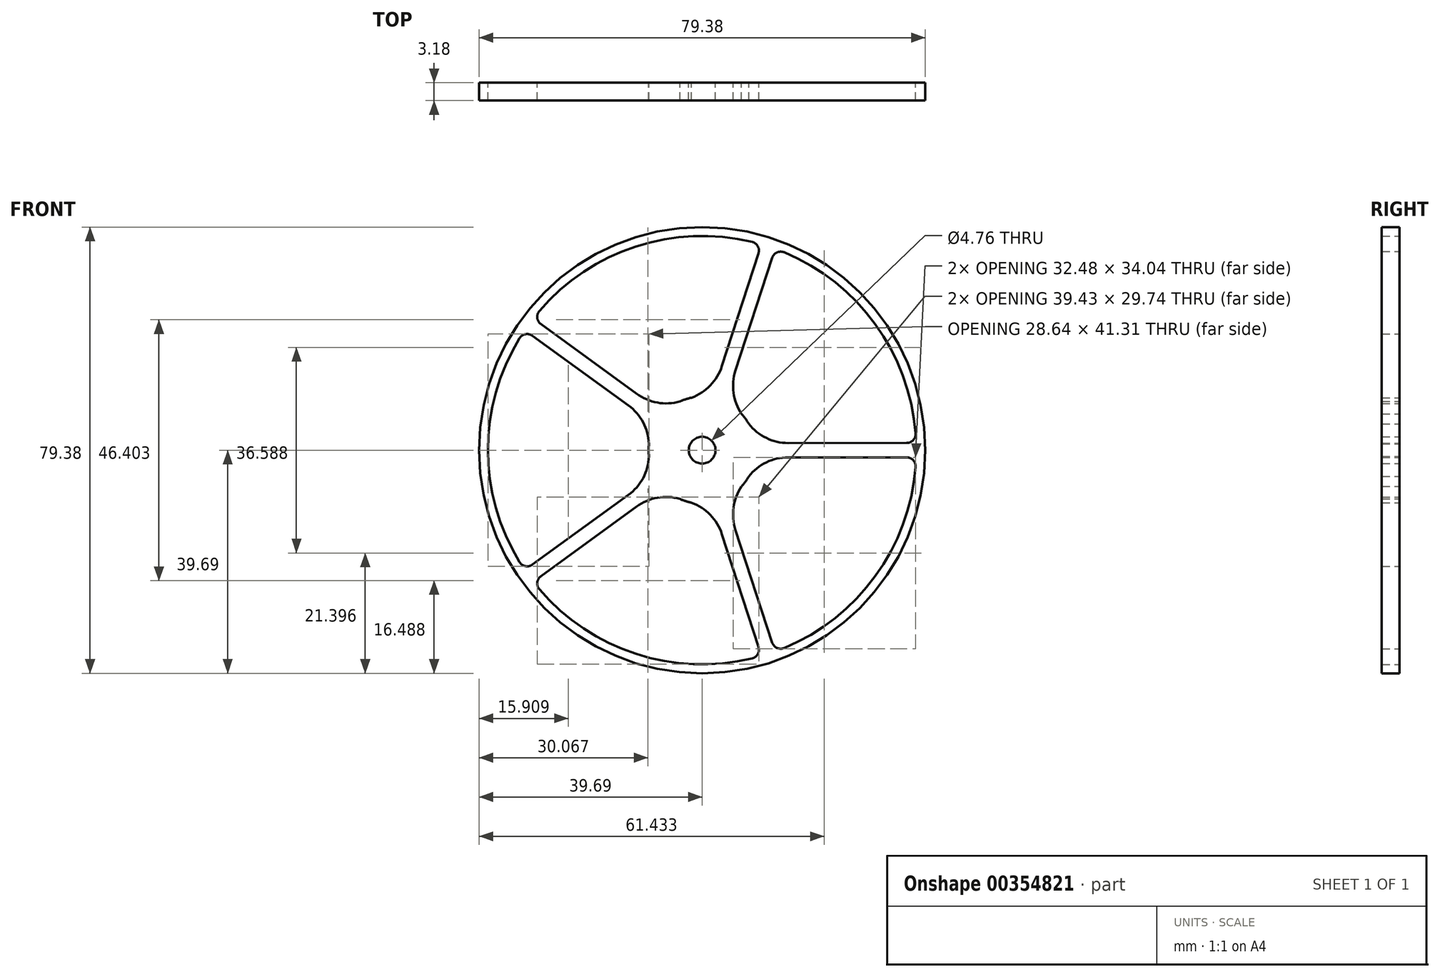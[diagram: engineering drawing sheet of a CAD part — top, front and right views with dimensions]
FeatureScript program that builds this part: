
annotation { "Feature Type Name" : "Feature", "Feature Type Description" : "" }
export const myFeature = defineFeature(function(context is Context, id is Id, definition is map)
    precondition{}
    {
        {
            var Q0;
            Q0=qCreatedBy(makeId("Front.planeOp"),FACE);
            var sketch = newSketch(context, id + "F0", { "sketchPlane" : qUnion([Q0])});
            skCircle(sketch, "E0", {"center": v(0, 0) * mm, "radius": 39.69 * mm});
            skArc(sketch, "E1", {"start": v(37.98, 3) * mm, "mid": v(30.82, 22.4) * mm, "end": v(14.59, 35.2) * mm});
            skArc(sketch, "E2", {"start": v(8.3, 4.68) * mm, "mid": v(7.7, 5.6) * mm, "end": v(7.01, 6.44) * mm});
            skCircle(sketch, "E3", {"center": v(0, 0) * mm, "radius": 2.38 * mm});
            skLineSegment(sketch, "E4.bottom", {"start": v(15.3, 1.27) * mm, "end": v(36.4, 1.29) * mm});
            skArc(sketch, "E5.filletArc", {"start": v(36.4, 1.29) * mm, "mid": v(37.57, 1.8) * mm, "end": v(37.98, 3) * mm});
            skArc(sketch, "E6", {"start": v(15.3, 1.27) * mm, "mid": v(11.4, 2.17) * mm, "end": v(8.3, 4.68) * mm});
            skLineSegment(sketch, "E7", {"start": v(0, 0) * mm, "end": v(50.05, 0) * mm, "construction": true});
            skArc(sketch, "E8.MirrorCS", {"start": v(15.3, -1.27) * mm, "mid": v(11.4, -2.17) * mm, "end": v(8.3, -4.68) * mm});
            skLineSegment(sketch, "E9.MirrorCS", {"start": v(15.3, -1.27) * mm, "end": v(36.4, -1.29) * mm});
            skArc(sketch, "E10.MirrorCS", {"start": v(36.4, -1.29) * mm, "mid": v(37.57, -1.8) * mm, "end": v(37.98, -3) * mm});
            skLineSegment(sketch, "E11.1.0", {"start": v(3.52, 14.94) * mm, "end": v(10.02, 35.02) * mm});
            skArc(sketch, "E11.1.1", {"start": v(3.52, 14.94) * mm, "mid": v(1.46, 11.52) * mm, "end": v(-1.89, 9.34) * mm});
            skArc(sketch, "E11.1.2", {"start": v(10.02, 35.02) * mm, "mid": v(9.9, 36.28) * mm, "end": v(8.88, 37.05) * mm});
            skArc(sketch, "E11.1.3", {"start": v(12.47, 34.22) * mm, "mid": v(13.32, 35.17) * mm, "end": v(14.59, 35.2) * mm});
            skLineSegment(sketch, "E11.1.4", {"start": v(5.94, 14.16) * mm, "end": v(12.47, 34.22) * mm});
            skArc(sketch, "E11.1.5", {"start": v(5.94, 14.16) * mm, "mid": v(5.59, 10.18) * mm, "end": v(7.01, 6.44) * mm});
            skLineSegment(sketch, "E11.2.0", {"start": v(-13.13, 7.96) * mm, "end": v(-30.2, 20.35) * mm});
            skArc(sketch, "E11.2.1", {"start": v(-13.13, 7.96) * mm, "mid": v(-10.5, 4.95) * mm, "end": v(-9.46, 1.1) * mm});
            skArc(sketch, "E11.2.2", {"start": v(-30.2, 20.35) * mm, "mid": v(-31.45, 20.63) * mm, "end": v(-32.5, 19.9) * mm});
            skArc(sketch, "E11.2.3", {"start": v(-28.7, 22.44) * mm, "mid": v(-29.33, 23.53) * mm, "end": v(-28.97, 24.75) * mm});
            skLineSegment(sketch, "E11.2.4", {"start": v(-11.63, 10.02) * mm, "end": v(-28.7, 22.44) * mm});
            skArc(sketch, "E11.2.5", {"start": v(-11.63, 10.02) * mm, "mid": v(-7.95, 8.46) * mm, "end": v(-3.96, 8.66) * mm});
            skLineSegment(sketch, "E11.3.0", {"start": v(-11.63, -10.02) * mm, "end": v(-28.7, -22.44) * mm});
            skArc(sketch, "E11.3.1", {"start": v(-11.63, -10.02) * mm, "mid": v(-7.95, -8.46) * mm, "end": v(-3.96, -8.66) * mm});
            skArc(sketch, "E11.3.2", {"start": v(-28.7, -22.44) * mm, "mid": v(-29.33, -23.53) * mm, "end": v(-28.97, -24.75) * mm});
            skArc(sketch, "E11.3.3", {"start": v(-30.2, -20.35) * mm, "mid": v(-31.45, -20.63) * mm, "end": v(-32.5, -19.9) * mm});
            skLineSegment(sketch, "E11.3.4", {"start": v(-13.13, -7.96) * mm, "end": v(-30.2, -20.35) * mm});
            skArc(sketch, "E11.3.5", {"start": v(-13.13, -7.96) * mm, "mid": v(-10.5, -4.95) * mm, "end": v(-9.46, -1.1) * mm});
            skLineSegment(sketch, "E11.4.0", {"start": v(5.94, -14.16) * mm, "end": v(12.47, -34.22) * mm});
            skArc(sketch, "E11.4.1", {"start": v(5.94, -14.16) * mm, "mid": v(5.59, -10.18) * mm, "end": v(7.01, -6.44) * mm});
            skArc(sketch, "E11.4.2", {"start": v(12.47, -34.22) * mm, "mid": v(13.32, -35.17) * mm, "end": v(14.59, -35.2) * mm});
            skArc(sketch, "E11.4.3", {"start": v(10.02, -35.02) * mm, "mid": v(9.9, -36.28) * mm, "end": v(8.88, -37.05) * mm});
            skLineSegment(sketch, "E11.4.4", {"start": v(3.52, -14.94) * mm, "end": v(10.02, -35.02) * mm});
            skArc(sketch, "E11.4.5", {"start": v(3.52, -14.94) * mm, "mid": v(1.46, -11.52) * mm, "end": v(-1.89, -9.34) * mm});
            skArc(sketch, "E12.trimOffspring", {"start": v(-32.5, 19.9) * mm, "mid": v(-38.1, 0) * mm, "end": v(-32.5, -19.9) * mm});
            skArc(sketch, "E13.trimOffspring", {"start": v(-28.97, -24.75) * mm, "mid": v(-11.77, -36.24) * mm, "end": v(8.88, -37.05) * mm});
            skArc(sketch, "E14.trimOffspring", {"start": v(14.59, -35.2) * mm, "mid": v(30.85, -22.35) * mm, "end": v(37.99, -2.9) * mm});
            skArc(sketch, "E15.trimOffspring", {"start": v(8.88, 37.05) * mm, "mid": v(-11.77, 36.24) * mm, "end": v(-28.97, 24.75) * mm});
            skArc(sketch, "E16.trimOffspring", {"start": v(-9.46, 1.1) * mm, "mid": v(-9.53, 0) * mm, "end": v(-9.46, -1.1) * mm});
            skArc(sketch, "E17.trimOffspring", {"start": v(-1.89, 9.34) * mm, "mid": v(-2.94, 9.06) * mm, "end": v(-3.96, 8.66) * mm});
            skArc(sketch, "E18.trimOffspring", {"start": v(7.01, -6.44) * mm, "mid": v(7.7, -5.6) * mm, "end": v(8.3, -4.68) * mm});
            skArc(sketch, "E19.trimOffspring", {"start": v(-3.96, -8.66) * mm, "mid": v(-2.94, -9.06) * mm, "end": v(-1.89, -9.34) * mm});
            skSolve(sketch);
        }
        {
            var Q0;
            Q0=makeQuery(id+"F0.imprint","IMPRINT",FACE,{"disambiguationData":[TD([[makeQuery(id+"F0.imprint","IMPRINT",EDGE,{"derivedFrom":sQuery(id+"F0.wireOp",EDGE,"E0")}),1.0]])]});
            extrude(context, id + "F1", {"entities" : qUnion([Q0]), "depth" : 3.17 * mm});
        }
    });
